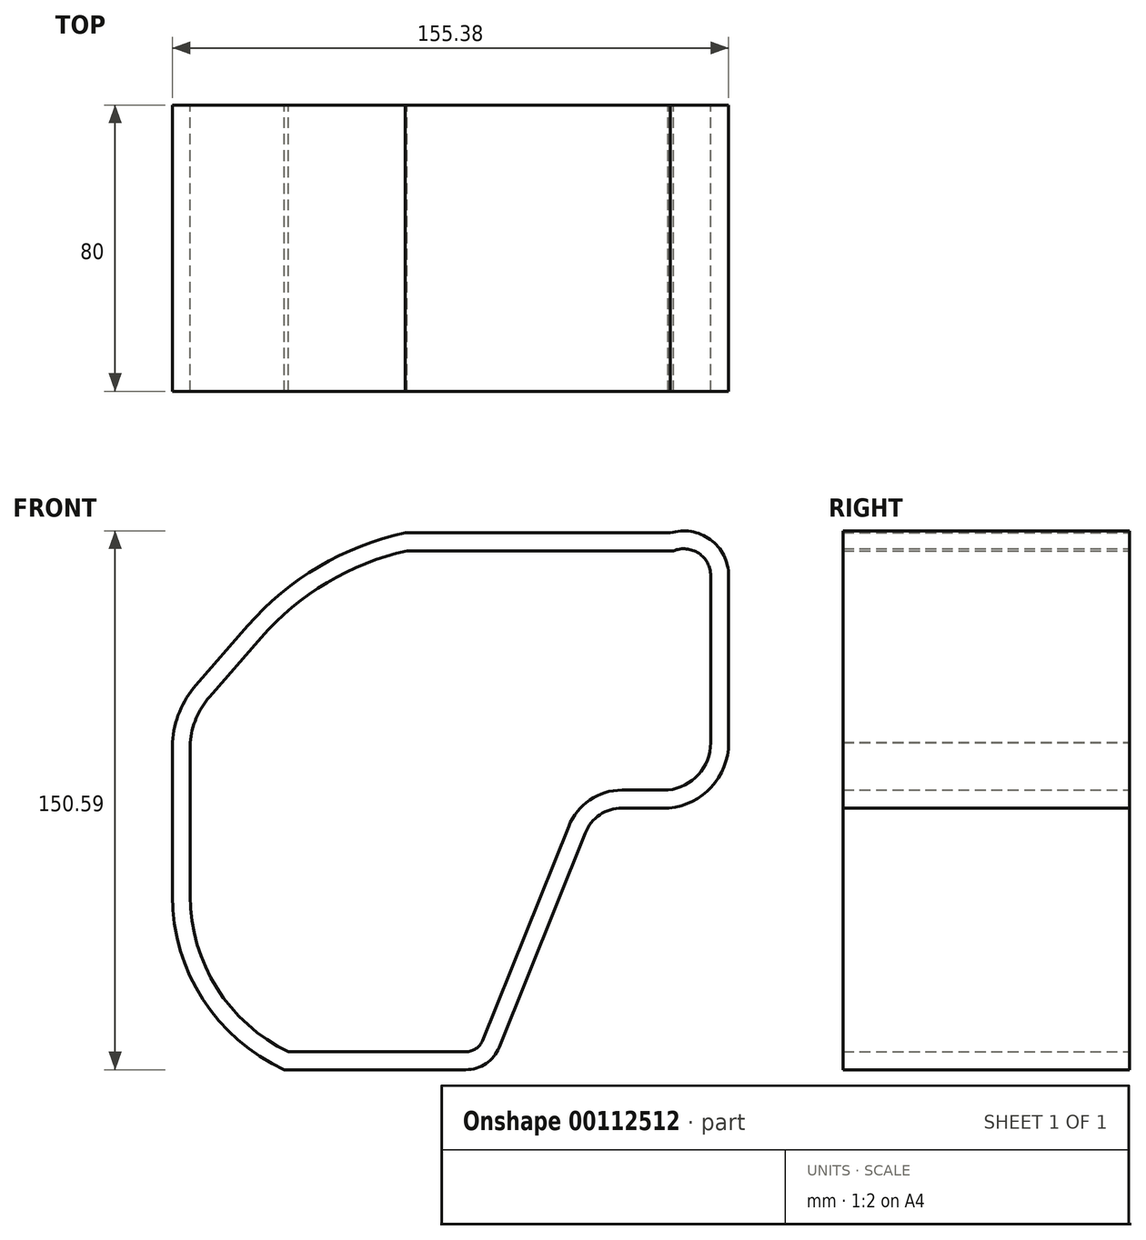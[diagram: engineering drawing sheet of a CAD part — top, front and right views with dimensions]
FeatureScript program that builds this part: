
annotation { "Feature Type Name" : "Feature", "Feature Type Description" : "" }
export const myFeature = defineFeature(function(context is Context, id is Id, definition is map)
    precondition{}
    {
        {
            var Q0;
            Q0=qCreatedBy(makeId("Front.planeOp"),FACE);
            var sketch = newSketch(context, id + "F0", { "sketchPlane" : qUnion([Q0])});
            skLineSegment(sketch, "E0", {"start": v(-124.27, -53.55) * mm, "end": v(-124.27, -18.8) * mm});
            skLineSegment(sketch, "E1", {"start": v(-119.74, -7.72) * mm, "end": v(-90.6, 46.83) * mm});
            skLineSegment(sketch, "E2", {"start": v(-72.4, 57.24) * mm, "end": v(99.83, 57.24) * mm});
            skLineSegment(sketch, "E3", {"start": v(109.9, 43.64) * mm, "end": v(109.9, -10.74) * mm});
            skLineSegment(sketch, "E4", {"start": v(26.3, -82.76) * mm, "end": v(-91.03, -82.76) * mm});
            skLineSegment(sketch, "E5", {"start": v(-122.76, -65.13) * mm, "end": v(-104.13, -79.23) * mm});
            skArc(sketch, "E6", {"start": v(-72.4, 57.24) * mm, "mid": v(-82.89, 54.45) * mm, "end": v(-90.6, 46.83) * mm});
            skArc(sketch, "E7", {"start": v(-119.74, -7.72) * mm, "mid": v(-123.1, -12.82) * mm, "end": v(-124.27, -18.8) * mm});
            skSolve(sketch);
        }
        {
            var Q0;
            Q0=qCreatedBy(makeId("Front.planeOp"),FACE);
            var sketch = newSketch(context, id + "F1", { "sketchPlane" : qUnion([Q0])});
            skLineSegment(sketch, "E8", {"start": v(-80.38, -18.96) * mm, "end": v(-80.38, 0) * mm});
            skLineSegment(sketch, "E9", {"start": v(-75, 12.86) * mm, "end": v(-60.58, 29.41) * mm});
            skLineSegment(sketch, "E10", {"start": v(-19.8, 53.65) * mm, "end": v(54.58, 53.65) * mm});
            skLineSegment(sketch, "E11", {"start": v(65, 46.72) * mm, "end": v(65, 0) * mm});
            skLineSegment(sketch, "E12", {"start": v(-3.38, -86.35) * mm, "end": v(-52.99, -86.35) * mm});
            skLineSegment(sketch, "E13", {"start": v(-80.38, -42.81) * mm, "end": v(-80.38, -27.74) * mm});
            skArc(sketch, "E14", {"start": v(-19.8, 53.65) * mm, "mid": v(-42.14, 44.8) * mm, "end": v(-60.58, 29.41) * mm});
            skArc(sketch, "E15", {"start": v(-75, 12.86) * mm, "mid": v(-78.73, 6.87) * mm, "end": v(-80.38, 0) * mm});
            skArc(sketch, "E16", {"start": v(-80.38, -42.81) * mm, "mid": v(-72.96, -68.53) * mm, "end": v(-52.99, -86.35) * mm});
            skLineSegment(sketch, "E17", {"start": v(1.26, -83.21) * mm, "end": v(25.33, -23.35) * mm});
            skLineSegment(sketch, "E18", {"start": v(40.25, -13.2) * mm, "end": v(53.08, -13.2) * mm});
            skLineSegment(sketch, "E19", {"start": v(-80.38, -18.96) * mm, "end": v(-80.38, -27.74) * mm});
            skArc(sketch, "E20", {"start": v(40.25, -13.2) * mm, "mid": v(31.22, -15.98) * mm, "end": v(25.33, -23.35) * mm});
            skArc(sketch, "E21", {"start": v(53.08, -13.2) * mm, "mid": v(61.58, -8.9) * mm, "end": v(65, 0) * mm});
            skPoint(sketch, "E22.visualSharp", {"position": v(0, -86.35) * mm});
            skArc(sketch, "E22.filletArc", {"start": v(-3.38, -86.35) * mm, "mid": v(-0.58, -85.5) * mm, "end": v(1.26, -83.21) * mm});
            skArc(sketch, "E23", {"start": v(65, 46.72) * mm, "mid": v(61.65, 52.98) * mm, "end": v(54.58, 53.65) * mm});
            skLineSegment(sketch, "E24.0", {"start": v(-20.34, 58.65) * mm, "end": v(53.7, 58.65) * mm});
            skArc(sketch, "E24.1", {"start": v(70, 46.72) * mm, "mid": v(64.88, 56.82) * mm, "end": v(53.7, 58.65) * mm});
            skLineSegment(sketch, "E24.2", {"start": v(70, 46.72) * mm, "end": v(70, 0) * mm});
            skArc(sketch, "E24.3", {"start": v(53.31, -18.2) * mm, "mid": v(65.2, -12.35) * mm, "end": v(70, 0) * mm});
            skLineSegment(sketch, "E24.4", {"start": v(40.25, -18.2) * mm, "end": v(53.31, -18.2) * mm});
            skLineSegment(sketch, "E24.5", {"start": v(-85.38, -18.96) * mm, "end": v(-85.38, -27.74) * mm});
            skLineSegment(sketch, "E24.6", {"start": v(-85.38, -18.96) * mm, "end": v(-85.38, 0.18) * mm});
            skArc(sketch, "E24.7", {"start": v(-78.77, 16.15) * mm, "mid": v(-83.38, 8.7) * mm, "end": v(-85.38, 0.18) * mm});
            skLineSegment(sketch, "E24.8", {"start": v(-78.77, 16.15) * mm, "end": v(-64.35, 32.7) * mm});
            skLineSegment(sketch, "E24.9", {"start": v(-85.38, -42.81) * mm, "end": v(-85.38, -27.74) * mm});
            skArc(sketch, "E24.10", {"start": v(-85.38, -42.81) * mm, "mid": v(-76.88, -71.68) * mm, "end": v(-54.1, -91.35) * mm});
            skLineSegment(sketch, "E24.11", {"start": v(-3.38, -91.35) * mm, "end": v(-54.1, -91.35) * mm});
            skArc(sketch, "E24.12", {"start": v(-3.38, -91.35) * mm, "mid": v(2.22, -89.63) * mm, "end": v(5.9, -85.08) * mm});
            skLineSegment(sketch, "E24.13", {"start": v(5.9, -85.08) * mm, "end": v(29.97, -25.2) * mm});
            skArc(sketch, "E24.14", {"start": v(-20.34, 58.65) * mm, "mid": v(-44.45, 49.24) * mm, "end": v(-64.35, 32.7) * mm});
            skArc(sketch, "E24.15", {"start": v(40.25, -18.2) * mm, "mid": v(34.03, -20.12) * mm, "end": v(29.97, -25.2) * mm});
            skSolve(sketch);
        }
        {
            var Q0;
            Q0=makeQuery(id+"F1.imprint","IMPRINT",FACE,{"disambiguationData":[TD([[makeQuery(id+"F1.imprint","IMPRINT",EDGE,{"derivedFrom":sQuery(id+"F1.wireOp",EDGE,"E8")}),1.0]])]});
            extrude(context, id + "F2", {"entities" : qUnion([Q0]), "depth" : 80 * mm});
        }
    });
